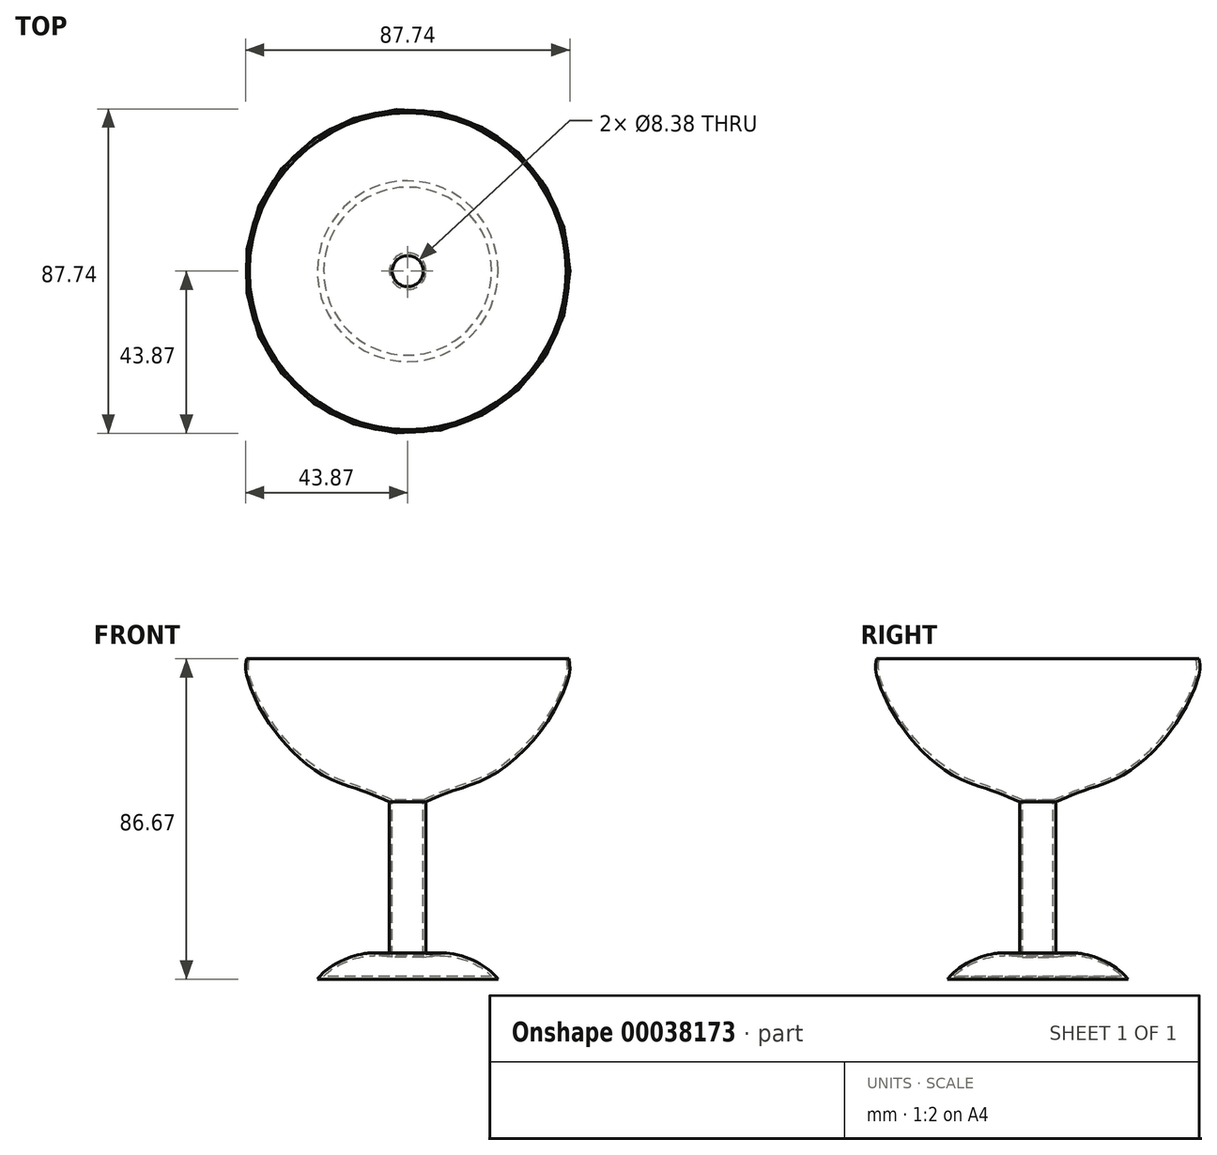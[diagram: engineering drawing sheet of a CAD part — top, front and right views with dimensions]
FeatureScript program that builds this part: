
annotation { "Feature Type Name" : "Feature", "Feature Type Description" : "" }
export const myFeature = defineFeature(function(context is Context, id is Id, definition is map)
    precondition{}
    {
        {
            var Q0;
            Q0=qCreatedBy(makeId("Front.planeOp"),FACE);
            var sketch = newSketch(context, id + "F0", { "sketchPlane" : qUnion([Q0])});
            skLineSegment(sketch, "E0", {"start": v(0, 42.25) * mm, "end": v(0, -44.42) * mm});
            skLineSegment(sketch, "E1", {"start": v(0, -44.42) * mm, "end": v(24.45, -44.42) * mm});
            skLineSegment(sketch, "E2", {"start": v(0, 42.25) * mm, "end": v(43.64, 42.25) * mm});
            skLineSegment(sketch, "E3", {"start": v(4.95, 3.56) * mm, "end": v(4.95, -37.6) * mm});
            skFitSpline(sketch, "E4", {"points": [v(43.64, 42.25) * mm, v(43.64, 37.92) * mm, v(37.76, 25.23) * mm, v(23.83, 11.3) * mm, v(11.76, 6.35) * mm, v(4.95, 3.56) * mm], "startDerivative": vector(5.92, -30.67) * mm, "endDerivative": vector(-36.16, -15.24) * mm});
            skPoint(sketch, "E5.1.internal.snap0", {"position": v(12.23, -44.42) * mm});
            skFitSpline(sketch, "E5", {"points": [v(4.95, -37.6) * mm, v(12.23, -37.6) * mm, v(20.74, -41.01) * mm, v(24.45, -44.42) * mm], "startDerivative": vector(20.59, 2.06) * mm, "endDerivative": vector(11, -12.26) * mm});
            skSolve(sketch);
        }
        {
            var Q0;
            Q0=makeQuery(id+"F0.imprint","IMPRINT",FACE,{"disambiguationData":[TD([[makeQuery(id+"F0.imprint","IMPRINT",EDGE,{"derivedFrom":sQuery(id+"F0.wireOp",EDGE,"E0")}),1.0]])]});
            var Q1;
            Q1=sQuery(id+"F0.wireOp",EDGE,"E0");
            revolve(context, id + "F1", {"entities" : qUnion([Q0]), "axis" : qUnion([Q1]), "revolveType" : RevolveType.FULL});
        }
        {
            var Q0;
            Q0=makeQuery(id+"F1.opRevolve","SWEPT_FACE",FACE,{"disambiguationData":[OSD([sQuery(id+"F0.wireOp",EDGE,"E2")])]});
            shell(context, id + "F2", {"entities" : qUnion([Q0]), "thickness" : 0.76 * mm});
        }
    });
